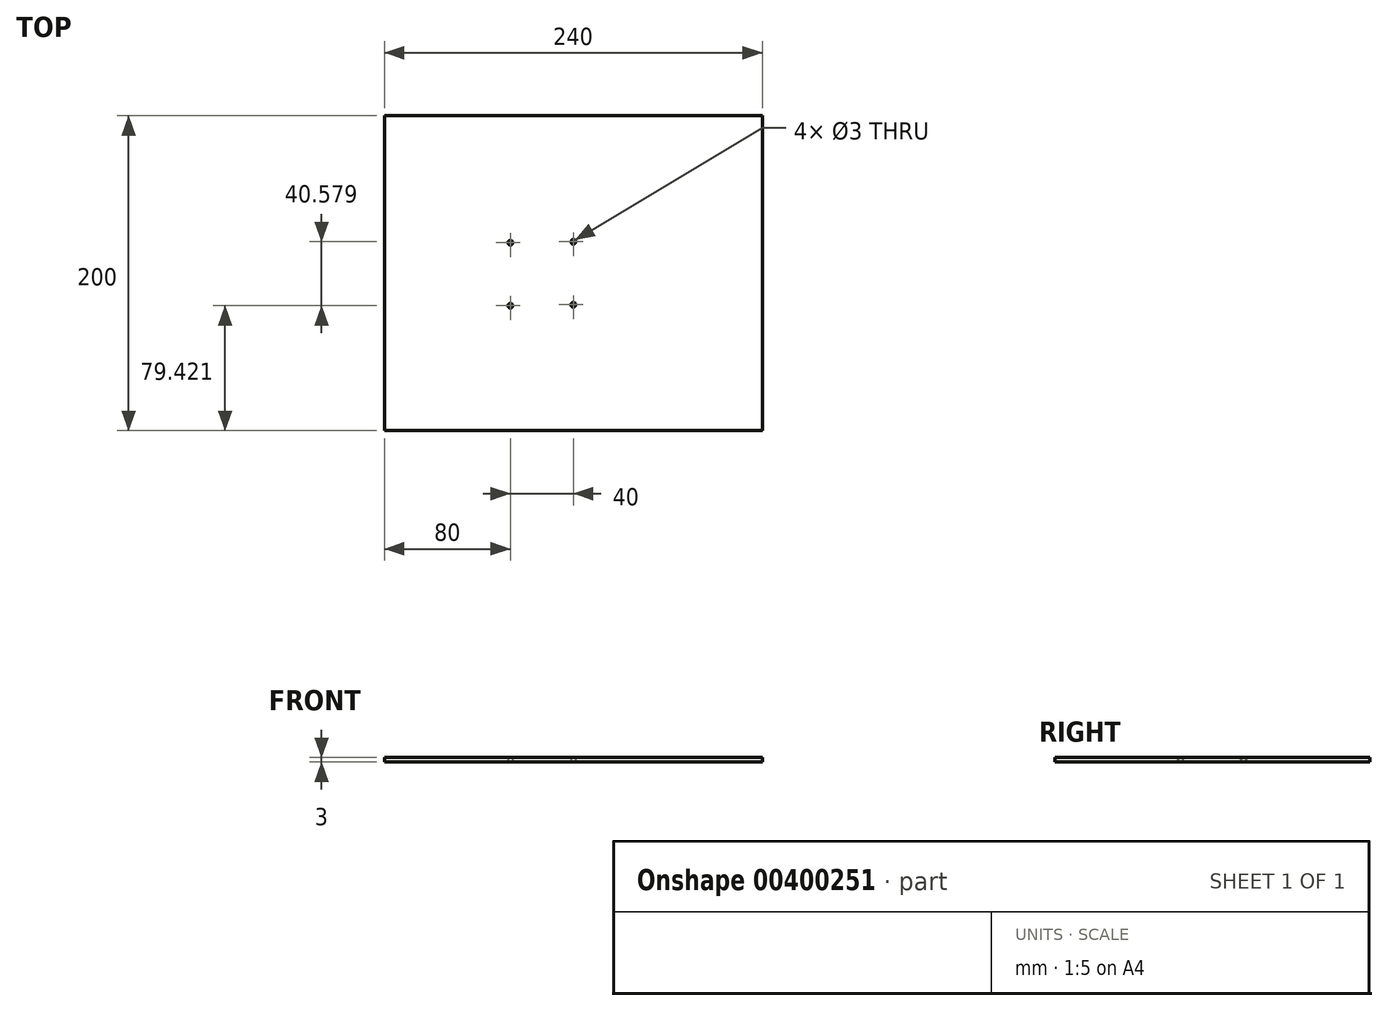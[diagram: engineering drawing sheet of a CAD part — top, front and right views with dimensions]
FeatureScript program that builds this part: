
annotation { "Feature Type Name" : "Feature", "Feature Type Description" : "" }
export const myFeature = defineFeature(function(context is Context, id is Id, definition is map)
    precondition{}
    {
        {
            var Q0;
            Q0=qCreatedBy(makeId("Top.planeOp"),FACE);
            var sketch = newSketch(context, id + "F0", { "sketchPlane" : qUnion([Q0])});
            skLineSegment(sketch, "E0.bottom", {"start": v(-100, 100) * mm, "end": v(100, 100) * mm});
            skLineSegment(sketch, "E0.top", {"start": v(-100, -100) * mm, "end": v(100, -100) * mm});
            skLineSegment(sketch, "E0.left", {"start": v(-100, 100) * mm, "end": v(-100, -100) * mm});
            skLineSegment(sketch, "E0.right", {"start": v(100, 100) * mm, "end": v(100, -100) * mm});
            skLineSegment(sketch, "E1.bottom", {"start": v(100, 100) * mm, "end": v(140, 100) * mm});
            skLineSegment(sketch, "E1.top", {"start": v(100, -100) * mm, "end": v(140, -100) * mm});
            skLineSegment(sketch, "E1.right", {"start": v(140, 100) * mm, "end": v(140, -100) * mm});
            skLineSegment(sketch, "E2", {"start": v(-34.06, 0) * mm, "end": v(33.54, 0) * mm, "construction": true});
            skLineSegment(sketch, "E3", {"start": v(0, -28.78) * mm, "end": v(0, 25.96) * mm, "construction": true});
            skCircle(sketch, "E4", {"center": v(-20, 19.42) * mm, "radius": 1.5 * mm});
            skCircle(sketch, "E5", {"center": v(20, 20) * mm, "radius": 1.5 * mm});
            skCircle(sketch, "E6", {"center": v(20, -20) * mm, "radius": 1.5 * mm});
            skCircle(sketch, "E7", {"center": v(-20, -20.58) * mm, "radius": 1.5 * mm});
            skSolve(sketch);
        }
        {
            var Q0;
            Q0 = qSketchRegion(id + "F0", true);
            extrude(context, id + "F1", {"entities" : qUnion([Q0]), "depth" : 3 * mm});
        }
    });
